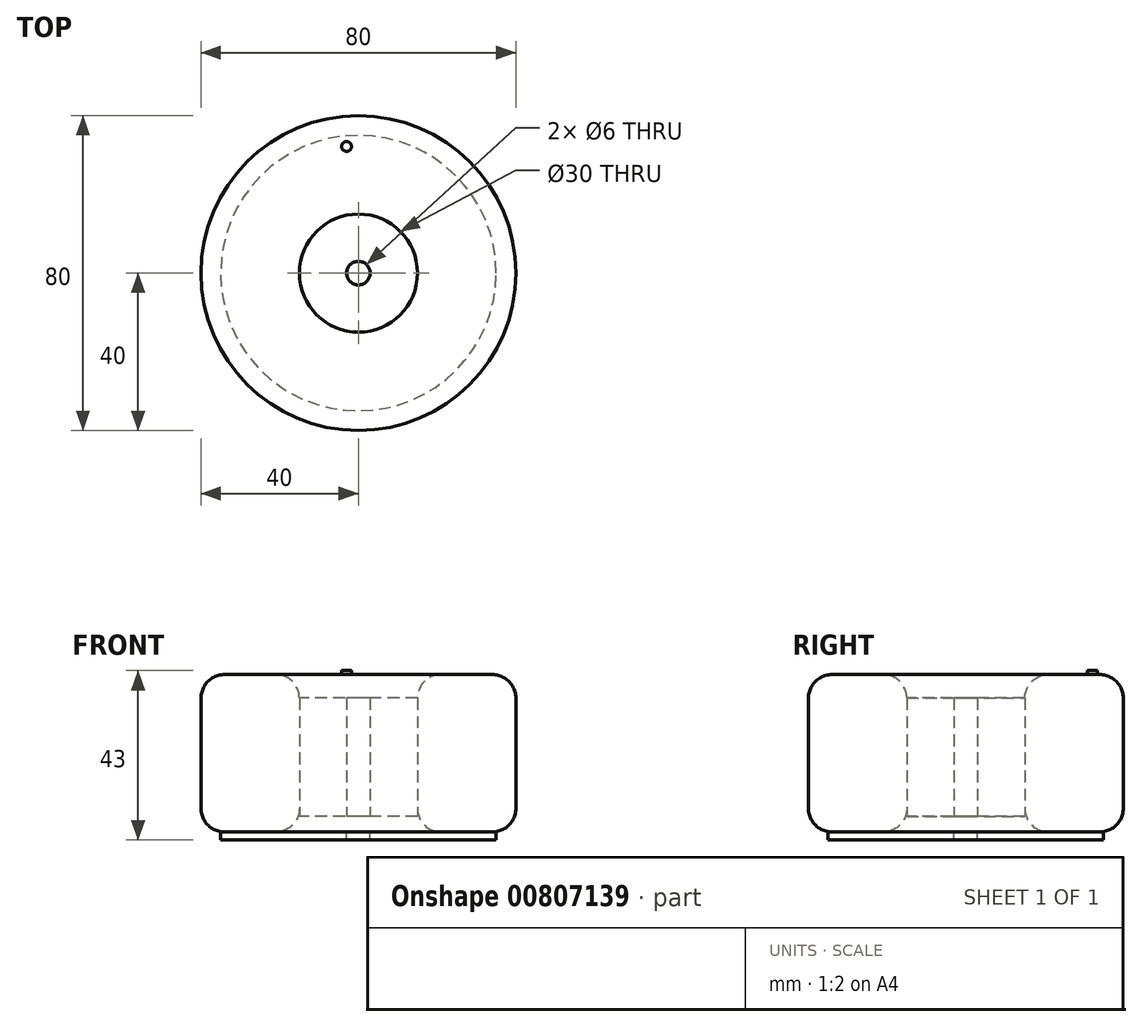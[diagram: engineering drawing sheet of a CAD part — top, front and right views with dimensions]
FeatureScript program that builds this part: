
annotation { "Feature Type Name" : "Feature", "Feature Type Description" : "" }
export const myFeature = defineFeature(function(context is Context, id is Id, definition is map)
    precondition{}
    {
        {
            var Q0;
            Q0=qCreatedBy(makeId("Top.planeOp"),FACE);
            var sketch = newSketch(context, id + "F0", { "sketchPlane" : qUnion([Q0])});
            skCircle(sketch, "E0", {"center": v(0, 0) * mm, "radius": 40 * mm});
            skCircle(sketch, "E1", {"center": v(0, 0) * mm, "radius": 15 * mm});
            skSolve(sketch);
        }
        {
            var Q0;
            Q0 = qSketchRegion(id + "F0", true);
            extrude(context, id + "F1", {"entities" : qUnion([Q0]), "depth" : 40 * mm, "offsetDistance" : 25 * mm});
        }
        {
            var Q0;
            Q0=makeQuery(id+"F1.opExtrude","CAP_EDGE",EDGE,{"disambiguationData":[OSD([sQuery(id+"F0.wireOp",EDGE,"E1")])],"isStart":false});
            var Q1;
            Q1=makeQuery(id+"F1.opExtrude","CAP_EDGE",EDGE,{"disambiguationData":[OSD([sQuery(id+"F0.wireOp",EDGE,"E0")])],"isStart":false});
            var Q2;
            Q2=makeQuery(id+"F1.opExtrude","CAP_EDGE",EDGE,{"disambiguationData":[OSD([sQuery(id+"F0.wireOp",EDGE,"E0")])],"isStart":true});
            var Q3;
            Q3=makeQuery(id+"F1.opExtrude","CAP_EDGE",EDGE,{"disambiguationData":[OSD([sQuery(id+"F0.wireOp",EDGE,"E1")])],"isStart":true});
            fillet(context, id + "F2", {"entities" : qUnion([Q0, Q1, Q2, Q3]), "radius" : 6 * mm, "tangentPropagation" : true, "allowEdgeOverflow" : false});
        }
        {
            var Q0;
            Q0=qCreatedBy(makeId("Top.planeOp"),FACE);
            cPlane(context, id + "F3", {"entities" : qUnion([Q0]), "cplaneType" : CPlaneType.OFFSET, "offset" : 4 * mm, "width" : 150 * mm, "height" : 150 * mm});
        }
        {
            var Q0;
            Q0=qCreatedBy(id+"F3.planeOp",FACE);
            var sketch = newSketch(context, id + "F4", { "sketchPlane" : qUnion([Q0])});
            skCircle(sketch, "E2.0", {"center": v(0, 0) * mm, "radius": 15 * mm});
            skCircle(sketch, "E3", {"center": v(0, 0) * mm, "radius": 3 * mm});
            skSolve(sketch);
        }
        {
            var Q0;
            Q0 = qSketchRegion(id + "F4", true);
            extrude(context, id + "F5", {"entities" : qUnion([Q0]), "depth" : 30 * mm, "offsetDistance" : 25 * mm});
        }
        {
            var Q0;
            Q0=makeQuery(id+"F1.opExtrude","CAP_FACE",FACE,{"disambiguationData":[OSD([sQuery(id+"F0.wireOp",EDGE,"E0"),sQuery(id+"F0.wireOp",EDGE,"E1")])],"isStart":false});
            var sketch = newSketch(context, id + "F6", { "sketchPlane" : qUnion([Q0])});
            skCircle(sketch, "E4", {"center": v(-3, 32.17) * mm, "radius": 1.25 * mm});
            skSolve(sketch);
        }
        {
            var Q0;
            Q0 = qSketchRegion(id + "F6", true);
            extrude(context, id + "F7", {"entities" : qUnion([Q0]), "depth" : 1 * mm, "offsetDistance" : 25 * mm});
        }
        {
            var Q0;
            Q0=makeQuery(id+"F1.opExtrude","CAP_FACE",FACE,{"disambiguationData":[OSD([sQuery(id+"F0.wireOp",EDGE,"E0"),sQuery(id+"F0.wireOp",EDGE,"E1")])],"isStart":true});
            var sketch = newSketch(context, id + "F8", { "sketchPlane" : qUnion([Q0])});
            skCircle(sketch, "E5", {"center": v(0, 0) * mm, "radius": 35 * mm});
            skCircle(sketch, "E6.0", {"center": v(0, 0) * mm, "radius": 3 * mm});
            skSolve(sketch);
        }
        {
            var Q0;
            Q0 = qSketchRegion(id + "F8", true);
            extrude(context, id + "F9", {"entities" : qUnion([Q0]), "depth" : 2 * mm, "offsetDistance" : 25 * mm});
        }
    });
